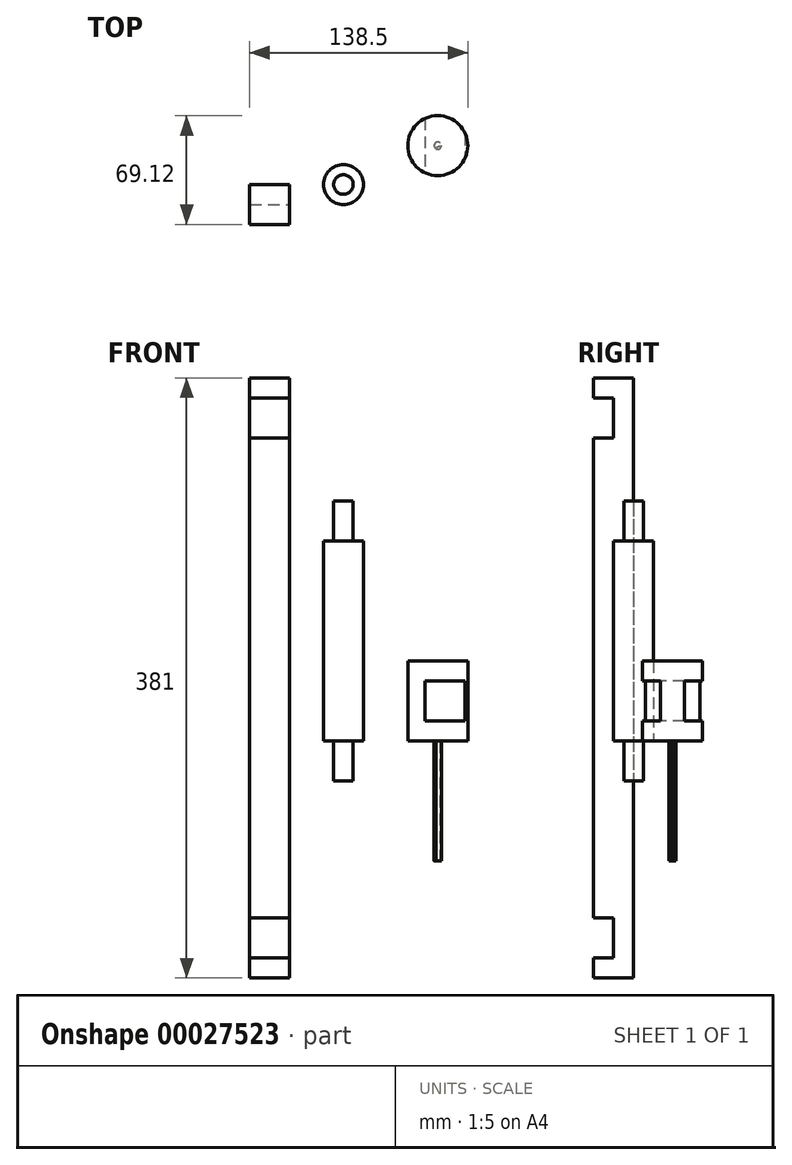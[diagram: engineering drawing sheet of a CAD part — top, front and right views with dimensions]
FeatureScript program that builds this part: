
annotation { "Feature Type Name" : "Feature", "Feature Type Description" : "" }
export const myFeature = defineFeature(function(context is Context, id is Id, definition is map)
    precondition{}
    {
        {
            var Q0;
            Q0=qCreatedBy(makeId("Top.planeOp"),FACE);
            var sketch = newSketch(context, id + "F0", { "sketchPlane" : qUnion([Q0])});
            skCircle(sketch, "E0", {"center": v(0, 0) * mm, "radius": 12.7 * mm});
            skSolve(sketch);
        }
        {
            var Q0;
            Q0=makeQuery(id+"F0.imprint","IMPRINT",FACE,{"disambiguationData":[TD([[makeQuery(id+"F0.imprint","IMPRINT",EDGE,{"derivedFrom":sQuery(id+"F0.wireOp",EDGE,"E0")}),1.0]])]});
            extrude(context, id + "F1", {"entities" : qUnion([Q0]), "depth" : 127 * mm});
        }
        {
            var Q0;
            Q0=makeQuery(id+"F1.opExtrude","CAP_FACE",FACE,{"disambiguationData":[OSD([sQuery(id+"F0.wireOp",EDGE,"E0")])],"isStart":false});
            var sketch = newSketch(context, id + "F2", { "sketchPlane" : qUnion([Q0])});
            skCircle(sketch, "E1", {"center": v(0, 0) * mm, "radius": 6.22 * mm});
            skSolve(sketch);
        }
        {
            var Q0;
            Q0=makeQuery(id+"F2.imprint","IMPRINT",FACE,{"disambiguationData":[TD([[makeQuery(id+"F2.imprint","IMPRINT",EDGE,{"derivedFrom":sQuery(id+"F2.wireOp",EDGE,"E1")}),1.0]])]});
            extrude(context, id + "F3", {"entities" : qUnion([Q0]), "operationType" : NewBodyOperationType.ADD, "depth" : 25.4 * mm});
        }
        {
            var Q0;
            Q0=makeQuery(id+"F1.opExtrude","CAP_FACE",FACE,{"disambiguationData":[OSD([sQuery(id+"F0.wireOp",EDGE,"E0")])],"isStart":true});
            var sketch = newSketch(context, id + "F4", { "sketchPlane" : qUnion([Q0])});
            skCircle(sketch, "E2", {"center": v(0, 0) * mm, "radius": 6.22 * mm});
            skSolve(sketch);
        }
        {
            var Q0;
            Q0=makeQuery(id+"F4.imprint","IMPRINT",FACE,{"disambiguationData":[TD([[makeQuery(id+"F4.imprint","IMPRINT",EDGE,{"derivedFrom":sQuery(id+"F4.wireOp",EDGE,"E2")}),1.0]])]});
            extrude(context, id + "F5", {"entities" : qUnion([Q0]), "operationType" : NewBodyOperationType.ADD, "depth" : 25.4 * mm});
        }
        {
            var Q0;
            Q0=qCreatedBy(makeId("Front.planeOp"),FACE);
            var sketch = newSketch(context, id + "F6", { "sketchPlane" : qUnion([Q0])});
            skLineSegment(sketch, "E3.bottom", {"start": v(-59.55, 230.6) * mm, "end": v(-34.15, 230.6) * mm});
            skLineSegment(sketch, "E3.top", {"start": v(-59.55, -150.4) * mm, "end": v(-34.15, -150.4) * mm});
            skLineSegment(sketch, "E3.left", {"start": v(-59.55, 230.6) * mm, "end": v(-59.55, -150.4) * mm});
            skLineSegment(sketch, "E3.right", {"start": v(-34.15, 230.6) * mm, "end": v(-34.15, -150.4) * mm});
            skSolve(sketch);
        }
        {
            var Q0;
            Q0=makeQuery(id+"F6.imprint","IMPRINT",FACE,{"disambiguationData":[TD([[makeQuery(id+"F6.imprint","IMPRINT",EDGE,{"derivedFrom":sQuery(id+"F6.wireOp",EDGE,"E3.bottom")}),-1.0]])]});
            extrude(context, id + "F7", {"entities" : qUnion([Q0]), "depth" : 25.4 * mm});
        }
        {
            var Q0;
            Q0=makeQuery(id+"F7.opExtrude","CAP_FACE",FACE,{"disambiguationData":[OSD([sQuery(id+"F6.wireOp",EDGE,"E3.bottom"),sQuery(id+"F6.wireOp",EDGE,"E3.top"),sQuery(id+"F6.wireOp",EDGE,"E3.left"),sQuery(id+"F6.wireOp",EDGE,"E3.right")])],"isStart":false});
            var sketch = newSketch(context, id + "F8", { "sketchPlane" : qUnion([Q0])});
            skLineSegment(sketch, "E4.bottom", {"start": v(-59.55, 217.9) * mm, "end": v(-34.15, 217.9) * mm});
            skLineSegment(sketch, "E4.top", {"start": v(-59.55, 192.5) * mm, "end": v(-34.15, 192.5) * mm});
            skLineSegment(sketch, "E4.left", {"start": v(-59.55, 217.9) * mm, "end": v(-59.55, 192.5) * mm});
            skLineSegment(sketch, "E4.right", {"start": v(-34.15, 217.9) * mm, "end": v(-34.15, 192.5) * mm});
            skLineSegment(sketch, "E5.bottom", {"start": v(-59.55, -112.3) * mm, "end": v(-34.15, -112.3) * mm});
            skLineSegment(sketch, "E5.top", {"start": v(-59.55, -137.7) * mm, "end": v(-34.15, -137.7) * mm});
            skLineSegment(sketch, "E5.left", {"start": v(-59.55, -112.3) * mm, "end": v(-59.55, -137.7) * mm});
            skLineSegment(sketch, "E5.right", {"start": v(-34.15, -112.3) * mm, "end": v(-34.15, -137.7) * mm});
            skSolve(sketch);
        }
        {
            var Q0;
            Q0=makeQuery(id+"F8.imprint","IMPRINT",FACE,{"disambiguationData":[TD([[makeQuery(id+"F8.imprint","IMPRINT",EDGE,{"derivedFrom":sQuery(id+"F8.wireOp",EDGE,"E4.bottom")}),-1.0]])]});
            var Q1;
            Q1=makeQuery(id+"F8.imprint","IMPRINT",FACE,{"disambiguationData":[TD([[makeQuery(id+"F8.imprint","IMPRINT",EDGE,{"derivedFrom":sQuery(id+"F8.wireOp",EDGE,"E5.bottom")}),-1.0]])]});
            extrude(context, id + "F9", {"entities" : qUnion([Q0, Q1]), "operationType" : NewBodyOperationType.REMOVE, "oppositeDirection" : true, "depth" : 12.7 * mm});
        }
        {
            var Q0;
            Q0=qCreatedBy(makeId("Top.planeOp"),FACE);
            var sketch = newSketch(context, id + "F10", { "sketchPlane" : qUnion([Q0])});
            skCircle(sketch, "E6", {"center": v(59.9, 24.67) * mm, "radius": 19.05 * mm});
            skSolve(sketch);
        }
        {
            var Q0;
            Q0=makeQuery(id+"F10.imprint","IMPRINT",FACE,{"disambiguationData":[TD([[makeQuery(id+"F10.imprint","IMPRINT",EDGE,{"derivedFrom":sQuery(id+"F10.wireOp",EDGE,"E6")}),1.0]])]});
            extrude(context, id + "F11", {"entities" : qUnion([Q0]), "depth" : 50.8 * mm});
        }
        {
            var Q0;
            Q0=qCreatedBy(makeId("Front.planeOp"),FACE);
            var sketch = newSketch(context, id + "F12", { "sketchPlane" : qUnion([Q0])});
            skLineSegment(sketch, "E7.bottom", {"start": v(51.94, 38.1) * mm, "end": v(77.34, 38.1) * mm});
            skLineSegment(sketch, "E7.top", {"start": v(51.94, 12.7) * mm, "end": v(77.34, 12.7) * mm});
            skLineSegment(sketch, "E7.left", {"start": v(51.94, 38.1) * mm, "end": v(51.94, 12.7) * mm});
            skLineSegment(sketch, "E7.right", {"start": v(77.34, 38.1) * mm, "end": v(77.34, 12.7) * mm});
            skSolve(sketch);
        }
        {
            var Q0;
            Q0=makeQuery(id+"F12.imprint","IMPRINT",FACE,{"disambiguationData":[TD([[makeQuery(id+"F12.imprint","IMPRINT",EDGE,{"derivedFrom":sQuery(id+"F12.wireOp",EDGE,"E7.bottom")}),-1.0]])]});
            extrude(context, id + "F13", {"entities" : qUnion([Q0]), "operationType" : NewBodyOperationType.REMOVE, "endBound" : BoundingType.THROUGH_ALL, "oppositeDirection" : true, "depth" : 25.4 * mm});
        }
        {
            var Q0;
            Q0=makeQuery(id+"F11.opExtrude","CAP_FACE",FACE,{"disambiguationData":[OSD([sQuery(id+"F10.wireOp",EDGE,"E6")])],"isStart":true});
            var sketch = newSketch(context, id + "F14", { "sketchPlane" : qUnion([Q0])});
            skCircle(sketch, "E8", {"center": v(59.9, -24.67) * mm, "radius": 2.27 * mm});
            skSolve(sketch);
        }
        {
            var Q0;
            Q0=makeQuery(id+"F14.imprint","IMPRINT",FACE,{"disambiguationData":[TD([[makeQuery(id+"F14.imprint","IMPRINT",EDGE,{"derivedFrom":sQuery(id+"F14.wireOp",EDGE,"E8")}),1.0]])]});
            extrude(context, id + "F15", {"entities" : qUnion([Q0]), "operationType" : NewBodyOperationType.ADD, "depth" : 76.2 * mm});
        }
        {
            var Q0;
            Q0=makeQuery(id+"F15.opExtrude","CAP_FACE",FACE,{"disambiguationData":[OSD([sQuery(id+"F14.wireOp",EDGE,"E8")])],"isStart":false});
            var sketch = newSketch(context, id + "F16", { "sketchPlane" : qUnion([Q0])});
            skFitSpline(sketch, "E9", {"points": [v(58.78, -22.7) * mm, v(59.96, -24.06) * mm, v(62.17, -24.6) * mm, v(61.44, -26.35) * mm, v(58.79, -26.66) * mm, v(57.63, -24.71) * mm, v(58.14, -23.24) * mm, v(58.78, -22.7) * mm]});
            skSolve(sketch);
        }
        {
            var Q0;
            {var subQ0=makeQuery(id+"F15.opExtrude","CAP_EDGE",EDGE,{"disambiguationData":[OSD([sQuery(id+"F14.wireOp",EDGE,"E8")])],"isStart":false});var subQ1=sQuery(id+"F16.wireOp",EDGE,"E9");var subQ7=makeQuery(id+"F16.imprint","INTERSECT",VERTEX,{"disambiguationData":[OD(0.0)],"derivedFrom":[subQ0,subQ1]});Q0=makeQuery(id+"F16.imprint","IMPRINT",FACE,{"disambiguationData":[TD([[makeQuery(id+"F16.imprint","IMPRINT",EDGE,{"disambiguationData":[TD([[subQ7,1.0]])],"derivedFrom":subQ1}),-1.0]])]});}
            extrude(context, id + "F17", {"entities" : qUnion([Q0]), "operationType" : NewBodyOperationType.REMOVE, "oppositeDirection" : true, "depth" : 76.2 * mm});
        }
    });
